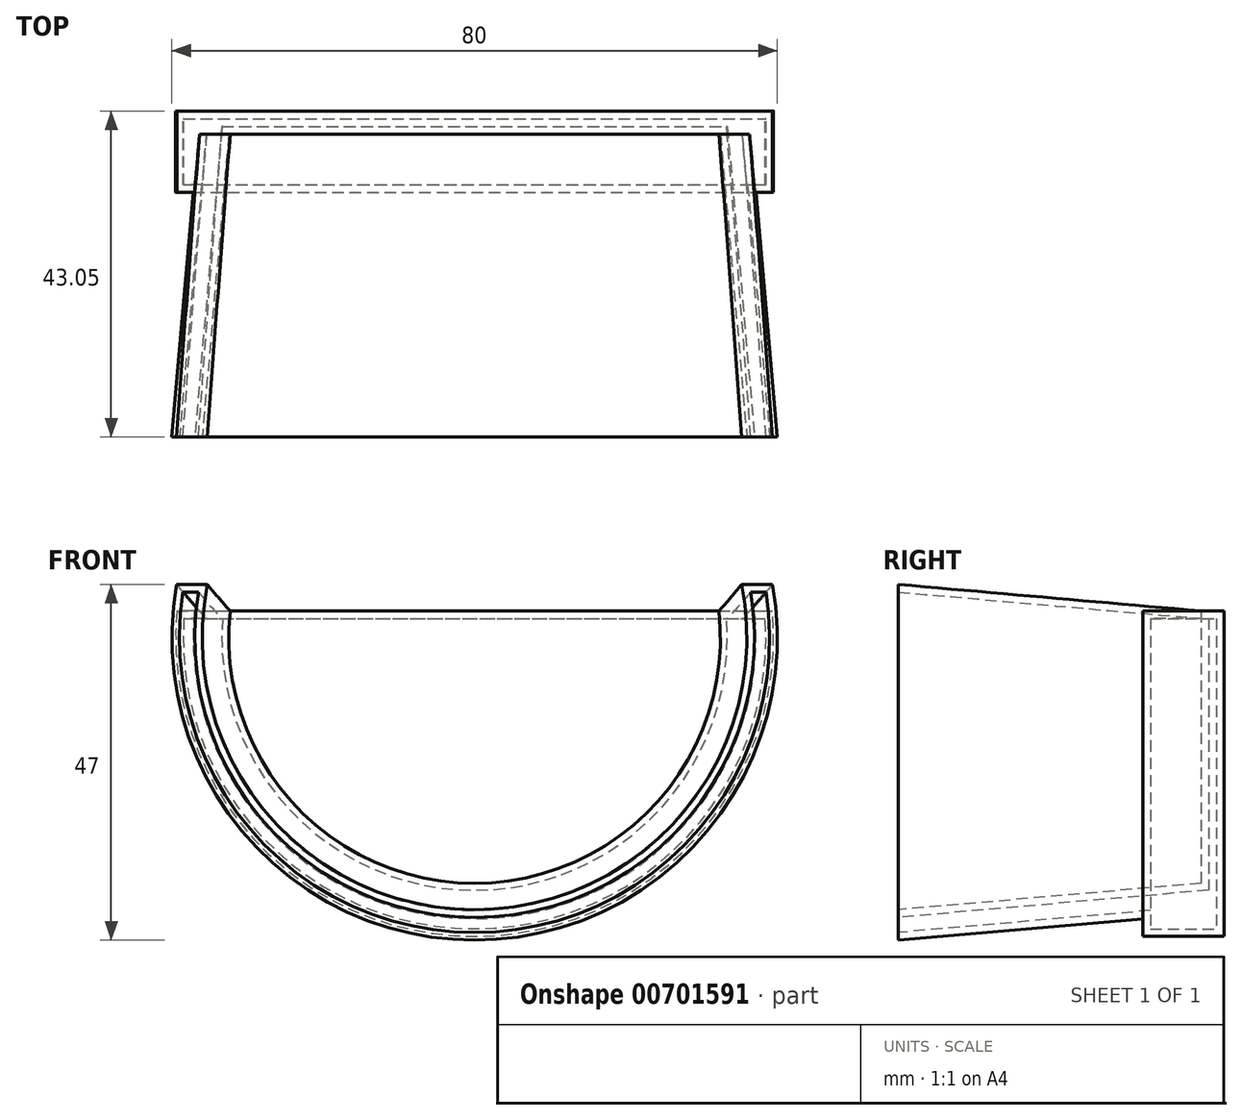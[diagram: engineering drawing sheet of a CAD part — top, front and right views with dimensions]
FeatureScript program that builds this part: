
annotation { "Feature Type Name" : "Feature", "Feature Type Description" : "" }
export const myFeature = defineFeature(function(context is Context, id is Id, definition is map)
    precondition{}
    {
        {
            var Q0;
            Q0=qCreatedBy(makeId("Front.planeOp"),FACE);
            var sketch = newSketch(context, id + "F0", { "sketchPlane" : qUnion([Q0])});
            skCircle(sketch, "E0", {"center": v(0, 0) * mm, "radius": 36.5 * mm});
            skLineSegment(sketch, "E1", {"start": v(-36.33, 3.5) * mm, "end": v(36.33, 3.5) * mm});
            skCircle(sketch, "E2", {"center": v(0, 0) * mm, "radius": 39.5 * mm});
            skLineSegment(sketch, "E3", {"start": v(36.33, 3.5) * mm, "end": v(39.34, 3.5) * mm});
            skLineSegment(sketch, "E4", {"start": v(-36.33, 3.5) * mm, "end": v(-39.34, 3.5) * mm});
            skSolve(sketch);
        }
        {
            var Q0;
            {var subQ0=sQuery(id+"F0.wireOp",EDGE,"E1");Q0=makeQuery(id+"F0.imprint","IMPRINT",FACE,{"disambiguationData":[TD([[makeQuery(id+"F0.imprint","IMPRINT",EDGE,{"derivedFrom":subQ0}),-1.0]])]});}
            extrude(context, id + "F1", {"entities" : qUnion([Q0]), "depth" : 40 * mm, "offsetDistance" : 25.4 * mm, "hasDraft" : true, "draftAngle" : 5 * degree});
        }
        {
            var Q0;
            Q0=makeQuery(id+"F1.opExtrude","CAP_FACE",FACE,{"disambiguationData":[OSD([sQuery(id+"F0.wireOp",EDGE,"E0"),sQuery(id+"F0.wireOp",EDGE,"E1")])],"isStart":false});
            var Q1;
            Q1=makeQuery(id+"F1.opExtrude","SWEPT_FACE",FACE,{"disambiguationData":[OSD([sQuery(id+"F0.wireOp",EDGE,"E1")])]});
            var Q2;
            Q2=makeQuery(id+"F1.opExtrude","CAP_FACE",FACE,{"disambiguationData":[OSD([sQuery(id+"F0.wireOp",EDGE,"E0"),sQuery(id+"F0.wireOp",EDGE,"E1")])],"isStart":true});
            shell(context, id + "F2", {"entities" : qUnion([Q0, Q1, Q2]), "thickness" : 4 * mm});
        }
        {
            var Q0;
            {var subQ3=sQuery(id+"F0.wireOp",EDGE,"E3");Q0=makeQuery(id+"F0.imprint","IMPRINT",FACE,{"disambiguationData":[TD([[makeQuery(id+"F0.imprint","IMPRINT",EDGE,{"derivedFrom":subQ3}),-1.0]])]});}
            extrude(context, id + "F3", {"entities" : qUnion([Q0]), "depth" : 7.7 * mm, "offsetDistance" : 25.4 * mm});
        }
        {
            var Q0;
            {var subQ0=sQuery(id+"F0.wireOp",EDGE,"E1");Q0=makeQuery(id+"F0.imprint","IMPRINT",FACE,{"disambiguationData":[TD([[makeQuery(id+"F0.imprint","IMPRINT",EDGE,{"derivedFrom":subQ0}),-1.0]])]});}
            var Q1;
            {var subQ3=sQuery(id+"F0.wireOp",EDGE,"E3");Q1=makeQuery(id+"F0.imprint","IMPRINT",FACE,{"disambiguationData":[TD([[makeQuery(id+"F0.imprint","IMPRINT",EDGE,{"derivedFrom":subQ3}),-1.0]])]});}
            extrude(context, id + "F4", {"entities" : qUnion([Q0, Q1]), "operationType" : NewBodyOperationType.ADD, "oppositeDirection" : true, "depth" : 3.05 * mm, "offsetDistance" : 25.4 * mm});
        }
        {
            var Q0;
            Q0=makeQuery(id+"F1.opExtrude","CAP_FACE",FACE,{"disambiguationData":[OSD([sQuery(id+"F0.wireOp",EDGE,"E0"),sQuery(id+"F0.wireOp",EDGE,"E1")])],"isStart":false});
            var Q1;
            Q1=makeQuery(id+"F1.opExtrude","SWEPT_BODY",BODY,{"disambiguationData":[OSD([sQuery(id+"F0.wireOp",EDGE,"E0"),sQuery(id+"F0.wireOp",EDGE,"E1")])]});
            shell(context, id + "F5", {"entities" : qUnion([Q0]), "parts" : qUnion([Q1]), "thickness" : 1 * mm});
        }
    });
